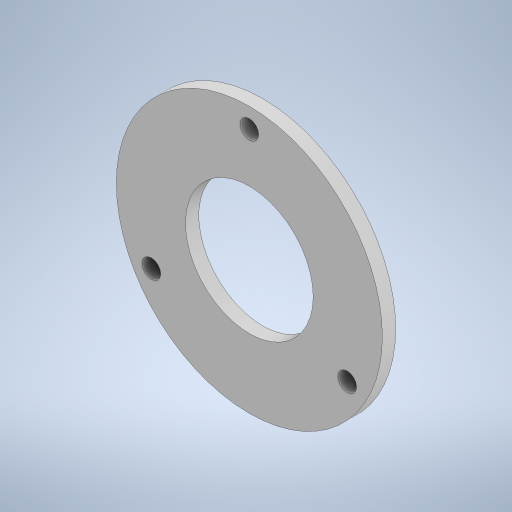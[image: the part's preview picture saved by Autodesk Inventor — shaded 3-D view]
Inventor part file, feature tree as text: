
AUTODESK INVENTOR PART (.ipt)
format: ipt  version: 2024 (Build 280153000, 153)  size: 241,152 bytes
history: native  units: mm
features: extrude x3, sketch x3
ambient origin geometry x8: Origin, YZ Plane, XZ Plane, XY Plane, X Axis, Y Axis, Z Axis, Center Point
bodies: Solid1 (feature_tree)
feature tree (6):
  extrude  "Extrusion1"  Depth=5.0mm TaperAngle=0.0deg
  extrude  "Extrusion2"  Depth=5.0mm TaperAngle=0.0deg
  extrude  "Extrusion3"  Depth=5.0mm
  sketch  "Sketch1"  dims[d0=100.0mm d1=5.0mm d2=0.0mm]
  sketch  "Sketch2"  dims[d3=48.0mm d4=5.0mm d5=0.0mm]
  sketch  "Sketch3"  dims[d6=7.0mm d8=4.0mm d9=30.0mm d11=360.0deg d13=5.0mm d14=0.0mm]
